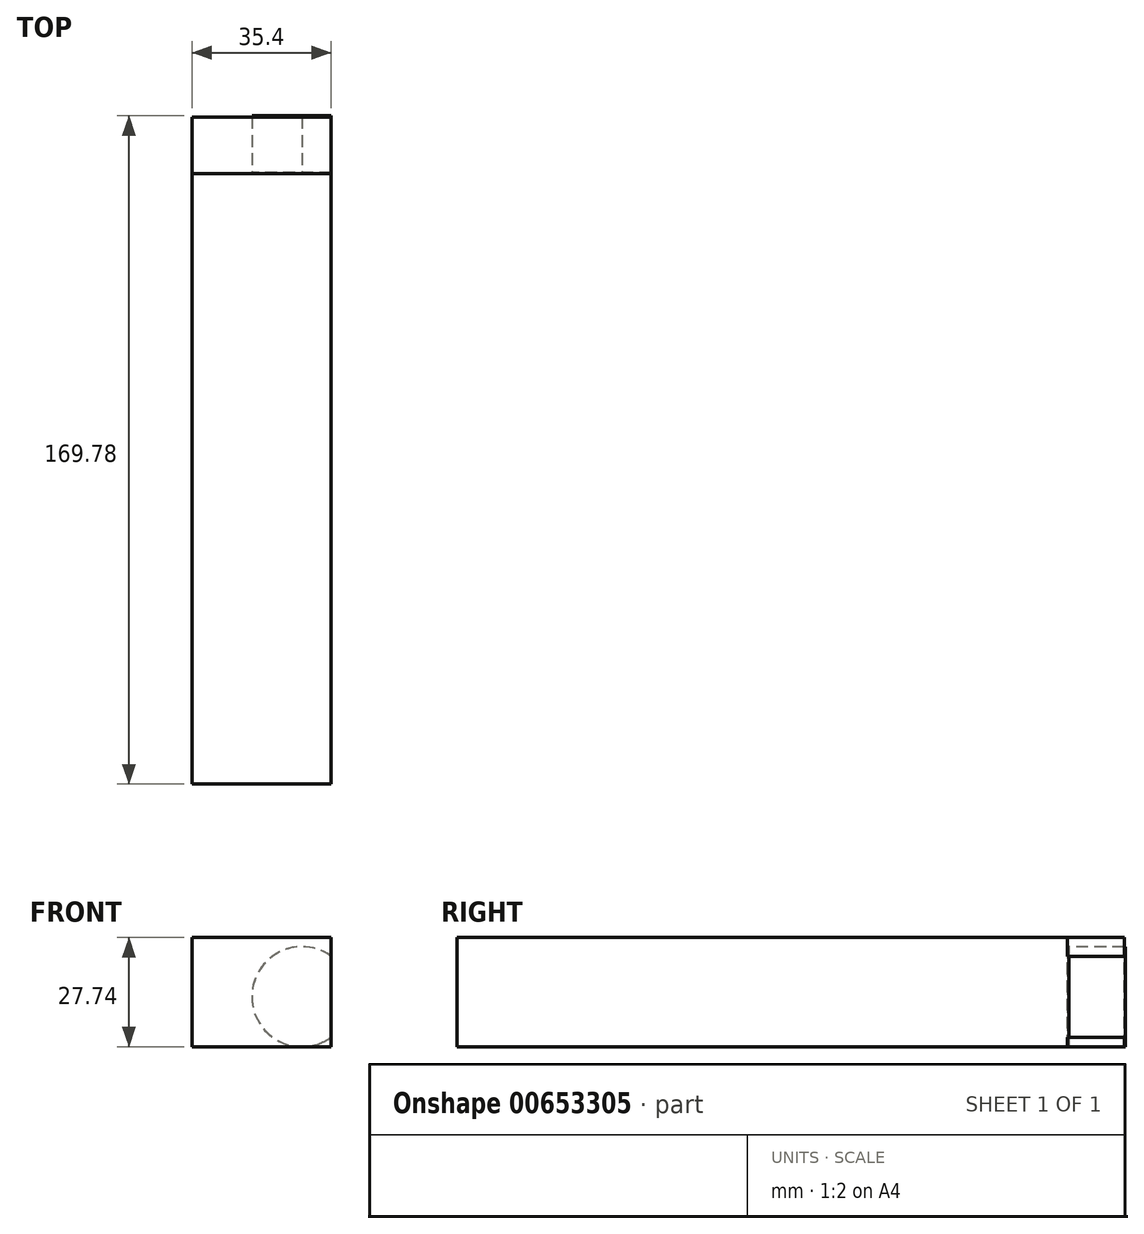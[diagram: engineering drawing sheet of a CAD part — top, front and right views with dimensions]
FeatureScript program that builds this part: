
annotation { "Feature Type Name" : "Feature", "Feature Type Description" : "" }
export const myFeature = defineFeature(function(context is Context, id is Id, definition is map)
    precondition{}
    {
        {
            var Q0;
            Q0=qCreatedBy(makeId("Front.planeOp"),FACE);
            var sketch = newSketch(context, id + "F0", { "sketchPlane" : qUnion([Q0])});
            skLineSegment(sketch, "E0.bottom", {"start": v(-16.2, 13.65) * mm, "end": v(19.2, 13.65) * mm});
            skLineSegment(sketch, "E0.top", {"start": v(-16.2, 41.4) * mm, "end": v(19.2, 41.4) * mm});
            skLineSegment(sketch, "E0.left", {"start": v(-16.2, 13.65) * mm, "end": v(-16.2, 41.4) * mm});
            skLineSegment(sketch, "E0.right", {"start": v(19.2, 13.65) * mm, "end": v(19.2, 41.4) * mm});
            skSolve(sketch);
        }
        {
            var Q0;
            Q0=makeQuery(id+"F0.imprint","IMPRINT",FACE,{"disambiguationData":[TD([[makeQuery(id+"F0.imprint","IMPRINT",EDGE,{"derivedFrom":sQuery(id+"F0.wireOp",EDGE,"E0.bottom")}),1.0]])]});
            extrude(context, id + "F1", {"entities" : qUnion([Q0]), "depth" : 155.07 * mm, "offsetDistance" : 25.4 * mm});
        }
        {
            var Q0;
            Q0=makeQuery(id+"F1.opExtrude","CAP_FACE",FACE,{"disambiguationData":[OSD([sQuery(id+"F0.wireOp",EDGE,"E0.bottom"),sQuery(id+"F0.wireOp",EDGE,"E0.top"),sQuery(id+"F0.wireOp",EDGE,"E0.left"),sQuery(id+"F0.wireOp",EDGE,"E0.right")])],"isStart":false});
            var sketch = newSketch(context, id + "F2", { "sketchPlane" : qUnion([Q0])});
            skCircle(sketch, "E1", {"center": v(11.74, 26.35) * mm, "radius": 12.7 * mm});
            skSolve(sketch);
        }
        {
            var Q0;
            {var subQ0=sQuery(id+"F2.wireOp",EDGE,"E1");var subQ1=makeQuery(id+"F1.opExtrude","CAP_EDGE",EDGE,{"disambiguationData":[OSD([sQuery(id+"F0.wireOp",EDGE,"E0.right")])],"isStart":false});var subQ2=makeQuery(id+"F2.imprint","INTERSECT",VERTEX,{"disambiguationData":[OD(0.0)],"derivedFrom":[subQ1,subQ0]});Q0=makeQuery(id+"F2.imprint","IMPRINT",FACE,{"disambiguationData":[TD([[makeQuery(id+"F2.imprint","IMPRINT",EDGE,{"disambiguationData":[TD([[subQ2,1.0]])],"derivedFrom":subQ0}),1.0]])]});}
            extrude(context, id + "F3", {"entities" : qUnion([Q0]), "operationType" : NewBodyOperationType.ADD, "oppositeDirection" : true, "depth" : 155.38 * mm, "offsetDistance" : 25.4 * mm, "hasSecondDirection" : true, "secondDirectionOppositeDirection" : true, "secondDirectionDepth" : 0 * mm});
        }
        {
            var Q0;
            Q0=makeQuery(id+"F1.opExtrude","CAP_FACE",FACE,{"disambiguationData":[OSD([sQuery(id+"F0.wireOp",EDGE,"E0.bottom"),sQuery(id+"F0.wireOp",EDGE,"E0.top"),sQuery(id+"F0.wireOp",EDGE,"E0.left"),sQuery(id+"F0.wireOp",EDGE,"E0.right")])],"isStart":true});
            var Q1;
            Q1=makeQuery(id+"F3.opExtrude","CAP_FACE",FACE,{"disambiguationData":[OSD([sQuery(id+"F0.wireOp",EDGE,"E0.right"),sQuery(id+"F2.wireOp",EDGE,"E1")])],"isStart":false});
            extrude(context, id + "F4", {"entities" : qUnion([Q0, Q1]), "operationType" : NewBodyOperationType.ADD, "depth" : 14.4 * mm, "offsetDistance" : 25.4 * mm});
        }
    });
